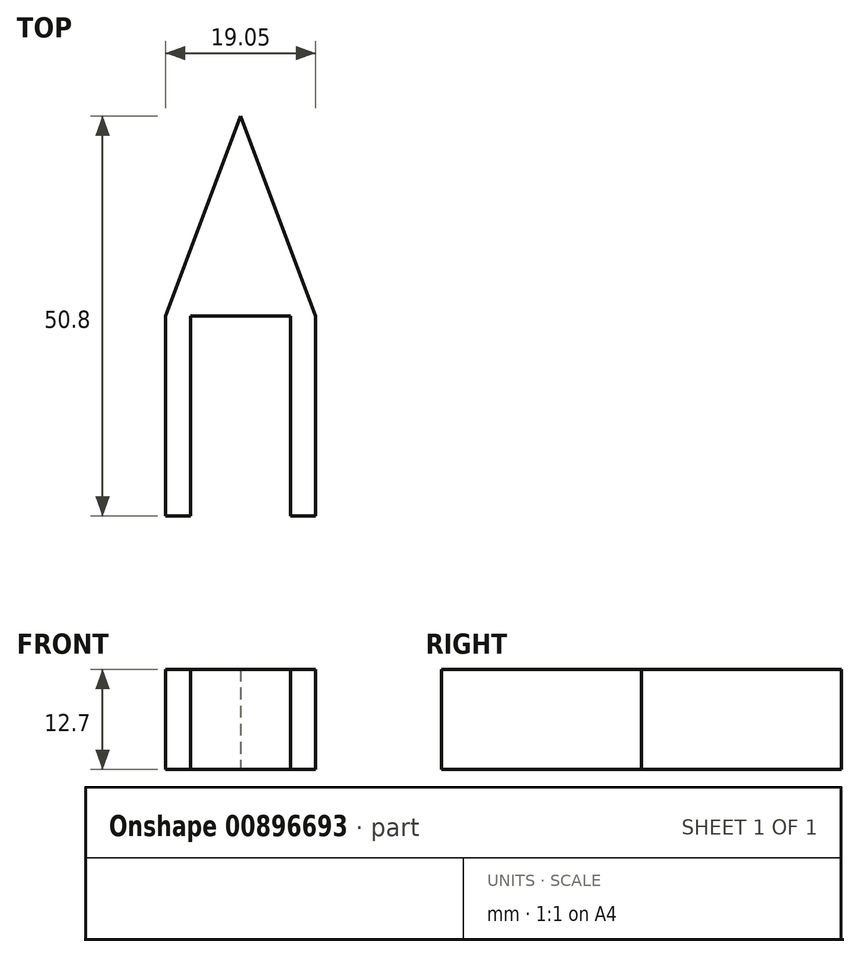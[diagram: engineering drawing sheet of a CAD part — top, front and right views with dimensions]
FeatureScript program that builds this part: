
annotation { "Feature Type Name" : "Feature", "Feature Type Description" : "" }
export const myFeature = defineFeature(function(context is Context, id is Id, definition is map)
    precondition{}
    {
        {
            var Q0;
            Q0=qCreatedBy(makeId("Top.planeOp"),FACE);
            var sketch = newSketch(context, id + "F0", { "sketchPlane" : qUnion([Q0])});
            skLineSegment(sketch, "E0.bottom", {"start": v(-44.17, -28.7) * mm, "end": v(-25.12, -28.7) * mm});
            skLineSegment(sketch, "E0.top", {"start": v(-44.17, 22.1) * mm, "end": v(-25.12, 22.1) * mm});
            skLineSegment(sketch, "E0.left", {"start": v(-44.17, -28.7) * mm, "end": v(-44.17, 22.1) * mm});
            skLineSegment(sketch, "E0.right", {"start": v(-25.12, -28.7) * mm, "end": v(-25.12, 22.1) * mm});
            skLineSegment(sketch, "E1.bottom", {"start": v(-41, -28.7) * mm, "end": v(-28.3, -28.7) * mm});
            skLineSegment(sketch, "E1.top", {"start": v(-41, -3.3) * mm, "end": v(-28.3, -3.3) * mm});
            skLineSegment(sketch, "E1.left", {"start": v(-41, -28.7) * mm, "end": v(-41, -3.3) * mm});
            skLineSegment(sketch, "E1.right", {"start": v(-28.3, -28.7) * mm, "end": v(-28.3, -3.3) * mm});
            skLineSegment(sketch, "E2", {"start": v(-41, -3.3) * mm, "end": v(-66.4, -3.3) * mm, "construction": true});
            skLineSegment(sketch, "E3", {"start": v(-28.3, -3.3) * mm, "end": v(-2.9, -3.3) * mm, "construction": true});
            skLineSegment(sketch, "E4", {"start": v(-34.65, 22.1) * mm, "end": v(-44.17, -3.3) * mm});
            skLineSegment(sketch, "E5", {"start": v(-34.65, 22.1) * mm, "end": v(-25.12, -3.3) * mm});
            skSolve(sketch);
        }
        {
            var Q0;
            Q0=makeQuery(id+"F0.imprint","IMPRINT",FACE,{"disambiguationData":[TD([[makeQuery(id+"F0.imprint","IMPRINT",EDGE,{"derivedFrom":sQuery(id+"F0.wireOp",EDGE,"E1.top")}),1.0]])]});
            extrude(context, id + "F1", {"entities" : qUnion([Q0]), "depth" : 12.7 * mm, "offsetDistance" : 25.4 * mm});
        }
    });
